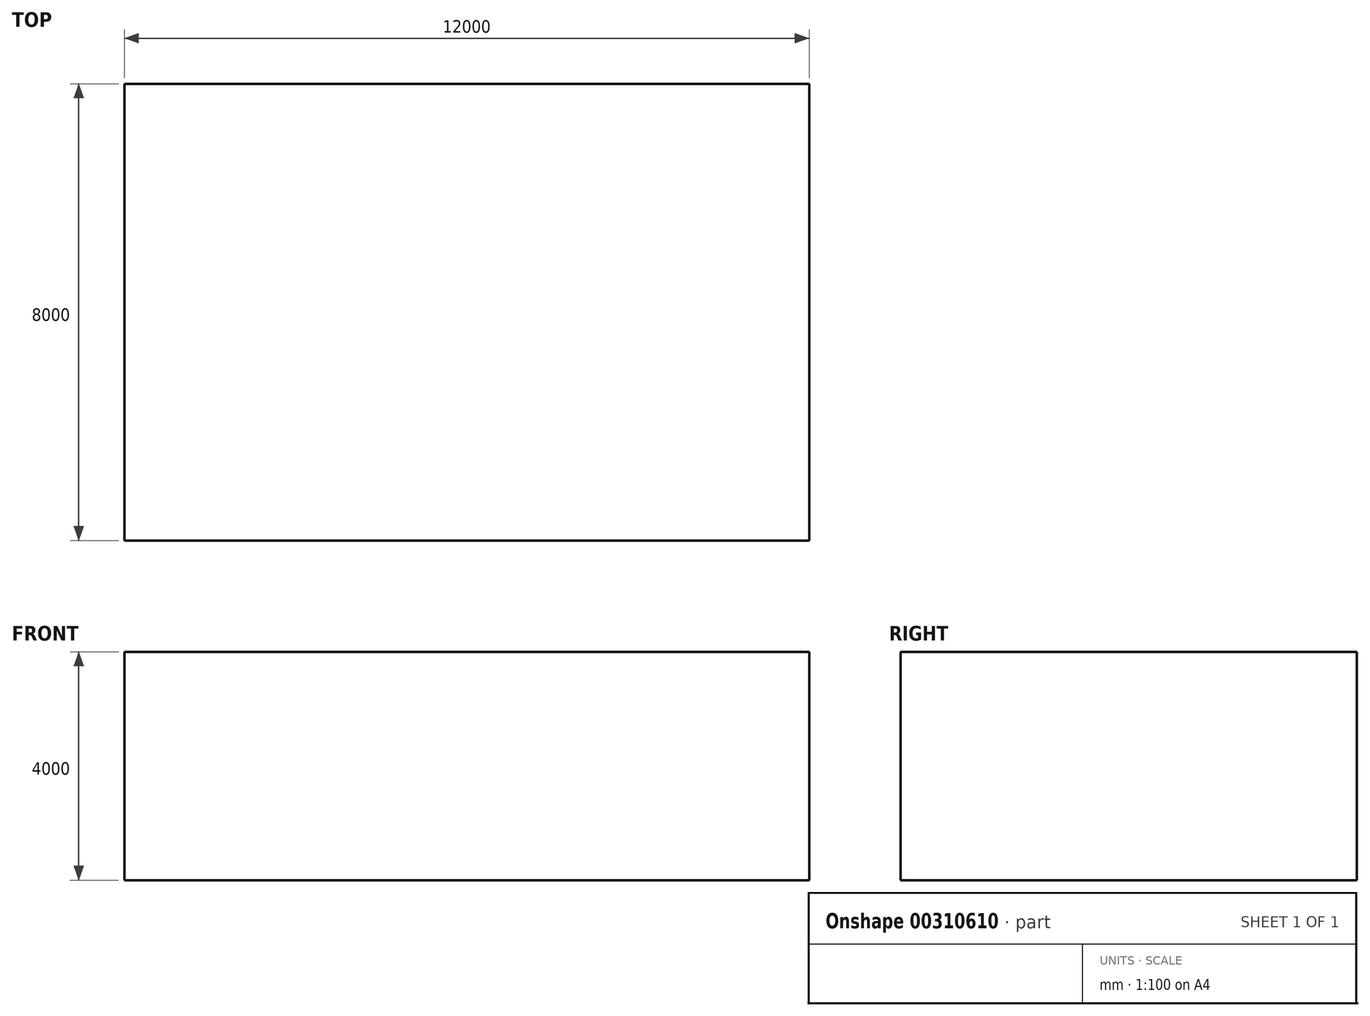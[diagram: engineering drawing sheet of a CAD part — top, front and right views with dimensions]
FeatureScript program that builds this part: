
annotation { "Feature Type Name" : "Feature", "Feature Type Description" : "" }
export const myFeature = defineFeature(function(context is Context, id is Id, definition is map)
    precondition{}
    {
        {
            var Q0;
            Q0=qCreatedBy(makeId("Right.planeOp"),FACE);
            var sketch = newSketch(context, id + "F0", { "sketchPlane" : qUnion([Q0])});
            skLineSegment(sketch, "E0.bottom", {"start": v(4000, -2000) * mm, "end": v(-4000, -2000) * mm});
            skLineSegment(sketch, "E0.left", {"start": v(4000, -2000) * mm, "end": v(4000, 2000) * mm});
            skLineSegment(sketch, "E0.right", {"start": v(-4000, -2000) * mm, "end": v(-4000, 2000) * mm});
            skPoint(sketch, "E0.middle", {"position": v(0, 0) * mm});
            skLineSegment(sketch, "E1", {"start": v(-4000, 2000) * mm, "end": v(0, 2000) * mm});
            skLineSegment(sketch, "E2", {"start": v(0, 2000) * mm, "end": v(4000, 2000) * mm});
            skSolve(sketch);
        }
        {
            var Q0;
            Q0 = qSketchRegion(id + "F0", true);
            extrude(context, id + "F1", {"entities" : qUnion([Q0]), "depth" : 12000 * mm});
        }
    });
